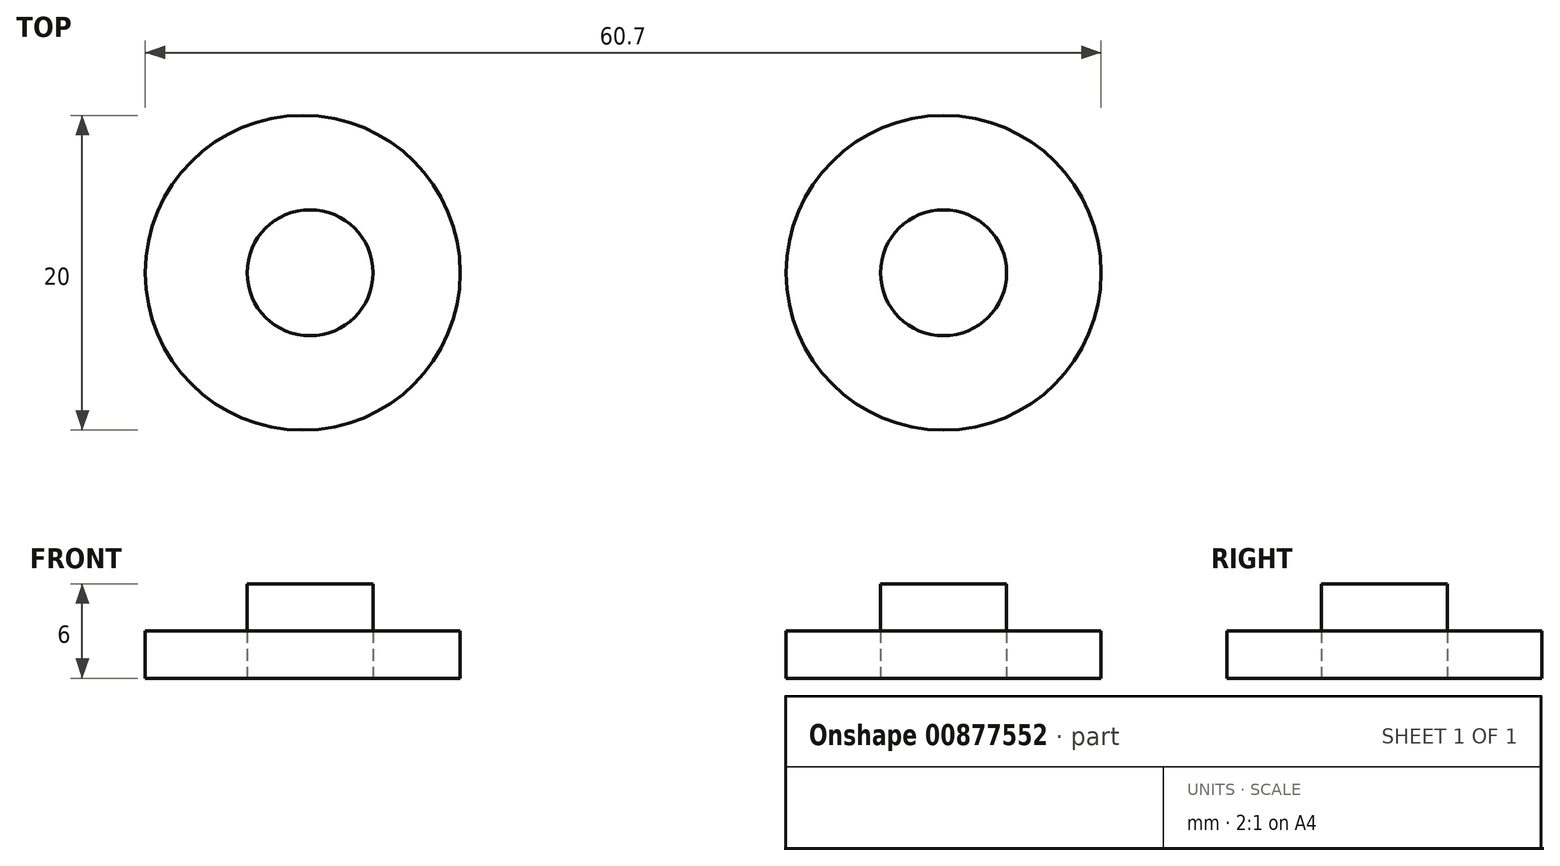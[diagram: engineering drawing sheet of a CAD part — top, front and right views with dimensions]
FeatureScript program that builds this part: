
annotation { "Feature Type Name" : "Feature", "Feature Type Description" : "" }
export const myFeature = defineFeature(function(context is Context, id is Id, definition is map)
    precondition{}
    {
        {
            var Q0;
            Q0=qCreatedBy(makeId("Top.planeOp"),FACE);
            var sketch = newSketch(context, id + "F0", { "sketchPlane" : qUnion([Q0])});
            skCircle(sketch, "E0", {"center": v(-15.7, 0) * mm, "radius": 10 * mm});
            skCircle(sketch, "E1", {"center": v(25, 0) * mm, "radius": 10 * mm});
            skSolve(sketch);
        }
        {
            var Q0;
            Q0=qCreatedBy(makeId("Top.planeOp"),FACE);
            var sketch = newSketch(context, id + "F1", { "sketchPlane" : qUnion([Q0])});
            skPoint(sketch, "E2.center.orphan", {"position": v(-15.23, 0) * mm});
            skCircle(sketch, "E3", {"center": v(25, 0) * mm, "radius": 4 * mm});
            skCircle(sketch, "E4", {"center": v(-15.23, 0) * mm, "radius": 4 * mm});
            skSolve(sketch);
        }
        {
            var Q0;
            Q0=makeQuery(id+"F0.imprint","IMPRINT",FACE,{"disambiguationData":[TD([[makeQuery(id+"F0.imprint","IMPRINT",EDGE,{"derivedFrom":sQuery(id+"F0.wireOp",EDGE,"E1")}),1.0]])]});
            var Q1;
            Q1=makeQuery(id+"F0.imprint","IMPRINT",FACE,{"disambiguationData":[TD([[makeQuery(id+"F0.imprint","IMPRINT",EDGE,{"derivedFrom":sQuery(id+"F0.wireOp",EDGE,"E0")}),1.0]])]});
            extrude(context, id + "F2", {"entities" : qUnion([Q0, Q1]), "depth" : 3 * mm, "offsetDistance" : 25 * mm});
        }
        {
            var Q0;
            Q0=makeQuery(id+"F1.imprint","IMPRINT",FACE,{"disambiguationData":[TD([[makeQuery(id+"F1.imprint","IMPRINT",EDGE,{"derivedFrom":sQuery(id+"F1.wireOp",EDGE,"E3")}),1.0]])]});
            var Q1;
            Q1=makeQuery(id+"F1.imprint","IMPRINT",FACE,{"disambiguationData":[TD([[makeQuery(id+"F1.imprint","IMPRINT",EDGE,{"derivedFrom":sQuery(id+"F1.wireOp",EDGE,"E4")}),1.0]])]});
            extrude(context, id + "F3", {"entities" : qUnion([Q0, Q1]), "depth" : 6 * mm, "offsetDistance" : 25 * mm});
        }
    });
